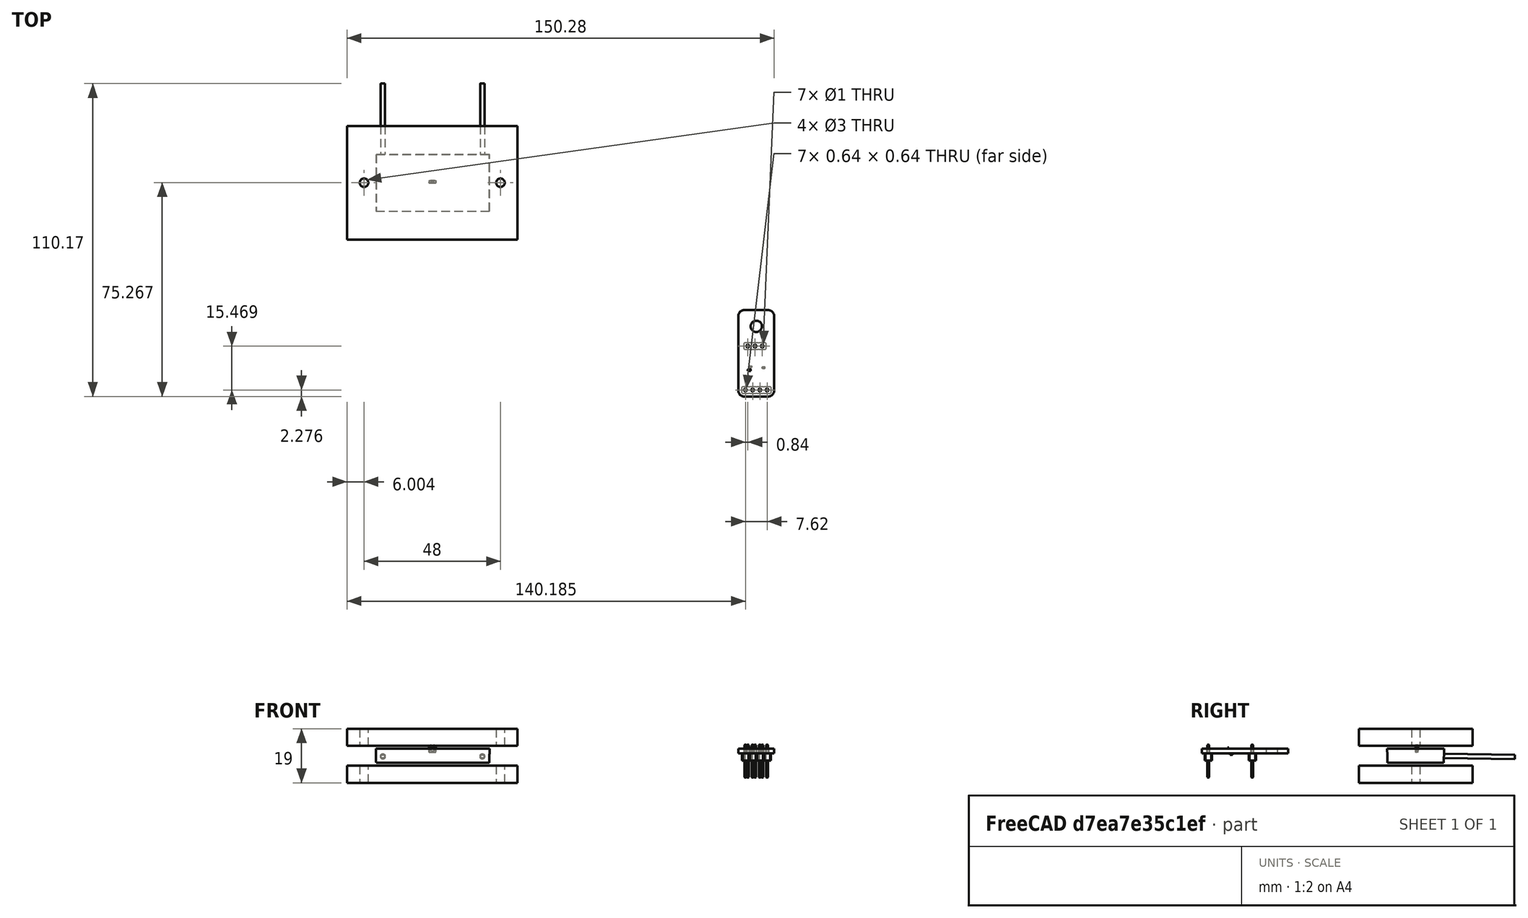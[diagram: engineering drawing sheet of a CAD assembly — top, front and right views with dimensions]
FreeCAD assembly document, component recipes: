
FREECAD ASSEMBLY — COMPONENT RECIPES ("Config-Peltier-SHT-31-rev01")

This assembly document has 4 components, labeled P0..P3 below (a component is one placed body or linked part). 3 of them carry a construction recipe — the FreeCAD feature program that regenerates the part from scratch, quoted from this document or its linked companion documents; the rest are supplied as boundary geometry only. No exploded tour is included for this assembly.
COMPONENT P0 — geometry summary ("SHT31-Breakout-rev01"; no construction recipe available for this part):
  bounding box: 30.4 x 12.6 x 3.0 mm
  tessellated surface: 10,052 triangles
  volume: 588 mm^3 (51% of its bounding box)
COMPONENT P1 — recipe-attached ("Placa-Sup", modeled in this document).
Construction recipe (the document's own serialized feature program — sketch geometry with constraints, then the solid features built on it; lengths are millimeters unless a unit is written):

FEATURE [Sketcher::SketchObject] Sketch
  FullyConstrained = true
  MapMode = 5
  Support = -> [XY_Plane]
  sketch-geometry (6):
    g0: Circle CenterX=-24.0764 CenterY=0.06715 CenterZ=0 NormalX=0 NormalY=0 NormalZ=1 AngleXU=0 Radius=1.5
    g1: Circle CenterX=23.9236 CenterY=0.06715 CenterZ=0 NormalX=0 NormalY=0 NormalZ=1 AngleXU=0 Radius=1.5
    g2: LineSegment StartX=-30.0764 StartY=20.0671 StartZ=0 EndX=29.9236 EndY=20.0671 EndZ=0
    g3: LineSegment StartX=29.9236 StartY=20.0671 StartZ=0 EndX=29.9236 EndY=-19.9329 EndZ=0
    g4: LineSegment StartX=29.9236 StartY=-19.9329 StartZ=0 EndX=-30.0764 EndY=-19.9329 EndZ=0
    g5: LineSegment StartX=-30.0764 StartY=-19.9329 StartZ=0 EndX=-30.0764 EndY=20.0671 EndZ=0
  constraints (18):
    c: Diameter(g1) = 3
    c: Diameter(g0) = 3
    c: Distance(g0,g-1) = 0.06715
    c: Coincident(g2,g3)
    c: Coincident(g3,g4)
    c: Coincident(g4,g5)
    c: Coincident(g5,g2)
    c: Horizontal(g2)
    c: Horizontal(g4)
    c: Vertical(g3)
    c: Vertical(g5)
    c: Distance(g3) = 40
    c: Distance(g2) = 60
    c: Distance(g1,g3) = 6
    c: Distance(g1,g2) = 20
    c: Distance(g0,g5) = 6
    c: Distance(g0,g2) = 20
    c: Block(g4)
FEATURE [PartDesign::Pad] Pad
  Direction = (0,0,1)
  Length = 6
  Length2 = 10
  Profile = -> Sketch
  ReferenceAxis = -> Sketch [N_Axis]
  Type = 0
FEATURE [PartDesign::Body] Body  label="Placa-Sup"
  Group = -> [Sketch,Pad]
  Origin = -> Origin
  Placement = pos=(0,0,1) rot=(0,0,1;0rad)
  Tip = -> Pad
COMPONENT P2 — recipe-attached ("Peltier", modeled in this document).
Construction recipe (the document's own serialized feature program — sketch geometry with constraints, then the solid features built on it; lengths are millimeters unless a unit is written):

FEATURE [PartDesign::Plane] DatumPlane
  Length = 60.9515
  MapMode = 5
  Placement = pos=(0,0,0) rot=(1,0,0;3.14159rad)
  ResizeMode = 0
  Width = 70.9193
FEATURE [Sketcher::SketchObject] Sketch002
  FullyConstrained = true
  MapMode = 5
  Placement = pos=(0,0,0) rot=(1,0,0;3.14159rad)
  Support = -> [DatumPlane]
  sketch-geometry (4):
    g0: LineSegment StartX=-19.909 StartY=9.99788 StartZ=0 EndX=20.091 EndY=9.99788 EndZ=0
    g1: LineSegment StartX=20.091 StartY=9.99788 StartZ=0 EndX=20.091 EndY=-10.0021 EndZ=0
    g2: LineSegment StartX=20.091 StartY=-10.0021 StartZ=0 EndX=-19.909 EndY=-10.0021 EndZ=0
    g3: LineSegment StartX=-19.909 StartY=-10.0021 StartZ=0 EndX=-19.909 EndY=9.99788 EndZ=0
  constraints (11):
    c: Coincident(g0,g1)
    c: Coincident(g1,g2)
    c: Coincident(g2,g3)
    c: Coincident(g3,g0)
    c: Horizontal(g0)
    c: Horizontal(g2)
    c: Vertical(g1)
    c: Vertical(g3)
    c: Distance(g0) = 40
    c: Distance(g1) = 20
    c: Block(g2)
FEATURE [PartDesign::Pad] Pad002
  Direction = (0,0,-1)
  Length = 5
  Length2 = 10
  Placement = pos=(0,0,0) rot=(1,0,0;3.14159rad)
  Profile = -> Sketch002
  ReferenceAxis = -> Sketch002 [N_Axis]
  TaperAngle = -1
  Type = 0
FEATURE [PartDesign::Plane] DatumPlane001
  Length = 61.1423
  MapMode = 45
  Placement = pos=(0.0910191,9.95852,-2.49818) rot=(0.58068,0.58068,0.570633;4.17868rad)
  ResizeMode = 0
  Support = -> [Pad002]
  Width = 60.1034
FEATURE [Sketcher::SketchObject] Sketch004
  FullyConstrained = true
  MapMode = 5
  Placement = pos=(0.0910191,9.95852,-2.49818) rot=(0.58068,0.58068,0.570633;4.17868rad)
  Support = -> [DatumPlane001]
  sketch-geometry (2):
    g0: Circle CenterX=0 CenterY=17.4497 CenterZ=0 NormalX=0 NormalY=0 NormalZ=1 AngleXU=0 Radius=0.75
    g1: Circle CenterX=0 CenterY=-17.5503 CenterZ=0 NormalX=0 NormalY=0 NormalZ=1 AngleXU=0 Radius=0.75
  constraints (6):
    c: Diameter(g0) = 1.5
    c: DistanceX(g-2,g0) = 0
    c: Block(g0)
    c: Diameter(g1) = 1.5
    c: DistanceX(g-2,g1) = 0
    c: DistanceY(g1,g0) = 35
FEATURE [PartDesign::Pad] Pad004
  BaseFeature = -> Pad002
  Direction = (0,0.999848,-0.0174524)
  Length = 25
  Length2 = 10
  Placement = pos=(0,0,0) rot=(1,0,0;3.14159rad)
  Profile = -> Sketch004
  ReferenceAxis = -> Sketch004 [N_Axis]
  Type = 0
FEATURE [PartDesign::Body] Body001  label="Peltier"
  Group = -> [DatumPlane,Sketch002,Pad002,DatumPlane001,Sketch004,Pad004]
  Origin = -> Origin001
  Tip = -> Pad004
COMPONENT P3 — recipe-attached ("Placa-Inf", modeled in this document).
Construction recipe (the document's own serialized feature program — sketch geometry with constraints, then the solid features built on it; lengths are millimeters unless a unit is written):

FEATURE [Sketcher::SketchObject] Sketch003
  FullyConstrained = true
  MapMode = 5
  Support = -> [XY_Plane002]
  sketch-geometry (6):
    g0: Circle CenterX=-24.0764 CenterY=0.06715 CenterZ=0 NormalX=0 NormalY=0 NormalZ=1 AngleXU=0 Radius=1.5
    g1: Circle CenterX=23.9236 CenterY=0.06715 CenterZ=0 NormalX=0 NormalY=0 NormalZ=1 AngleXU=0 Radius=1.5
    g2: LineSegment StartX=-30.0764 StartY=20.0671 StartZ=0 EndX=29.9236 EndY=20.0671 EndZ=0
    g3: LineSegment StartX=29.9236 StartY=20.0671 StartZ=0 EndX=29.9236 EndY=-19.9329 EndZ=0
    g4: LineSegment StartX=29.9236 StartY=-19.9329 StartZ=0 EndX=-30.0764 EndY=-19.9329 EndZ=0
    g5: LineSegment StartX=-30.0764 StartY=-19.9329 StartZ=0 EndX=-30.0764 EndY=20.0671 EndZ=0
  constraints (18):
    c: Diameter(g1) = 3
    c: Diameter(g0) = 3
    c: Distance(g0,g-1) = 0.06715
    c: Coincident(g2,g3)
    c: Coincident(g3,g4)
    c: Coincident(g4,g5)
    c: Coincident(g5,g2)
    c: Horizontal(g2)
    c: Horizontal(g4)
    c: Vertical(g3)
    c: Vertical(g5)
    c: Distance(g3) = 40
    c: Distance(g2) = 60
    c: Distance(g1,g3) = 6
    c: Distance(g1,g2) = 20
    c: Distance(g0,g5) = 6
    c: Distance(g0,g2) = 20
    c: Block(g4)
FEATURE [PartDesign::Pad] Pad003
  Direction = (0,0,1)
  Length = 6
  Length2 = 10
  Profile = -> Sketch003
  ReferenceAxis = -> Sketch003 [N_Axis]
  Type = 0
FEATURE [PartDesign::Body] Body002  label="Placa-Inf"
  Group = -> [Sketch003,Pad003]
  Origin = -> Origin002
  Placement = pos=(0,0,-12) rot=(0,0,1;0rad)
  Tip = -> Pad003
PROVENANCE & LICENSES
A FreeCAD (.FCStd) document from a public repository crawl; recipes are the document's own serialized feature recipes (and, for linked parts, companion documents' recipes).
License: mit.
